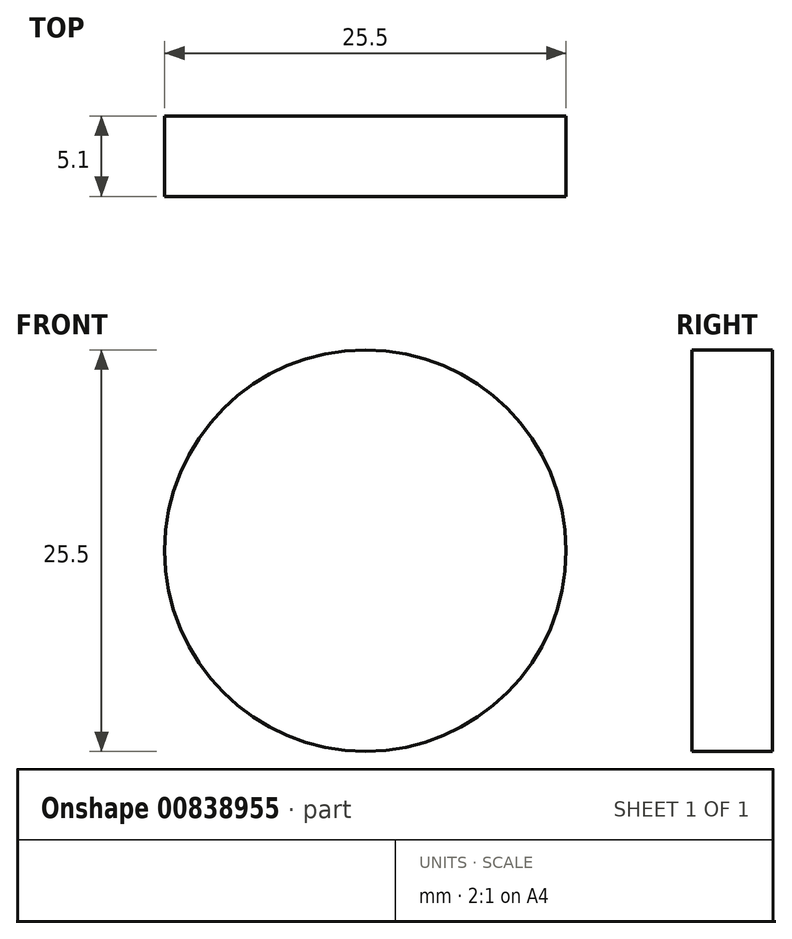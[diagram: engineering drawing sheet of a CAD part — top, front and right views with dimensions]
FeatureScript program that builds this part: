
annotation { "Feature Type Name" : "Feature", "Feature Type Description" : "" }
export const myFeature = defineFeature(function(context is Context, id is Id, definition is map)
    precondition{}
    {
        {
            var Q0;
            Q0=qCreatedBy(makeId("Front.planeOp"),FACE);
            var sketch = newSketch(context, id + "F0", { "sketchPlane" : qUnion([Q0])});
            skCircle(sketch, "E0", {"center": v(0, 0) * mm, "radius": 12.75 * mm});
            skSolve(sketch);
        }
        {
            var Q0;
            Q0=makeQuery(id+"F0.imprint","IMPRINT",FACE,{"disambiguationData":[TD([[makeQuery(id+"F0.imprint","IMPRINT",EDGE,{"derivedFrom":sQuery(id+"F0.wireOp",EDGE,"E0")}),1.0]])]});
            extrude(context, id + "F1", {"entities" : qUnion([Q0]), "depth" : 5.1 * mm, "offsetDistance" : 25 * mm});
        }
    });
